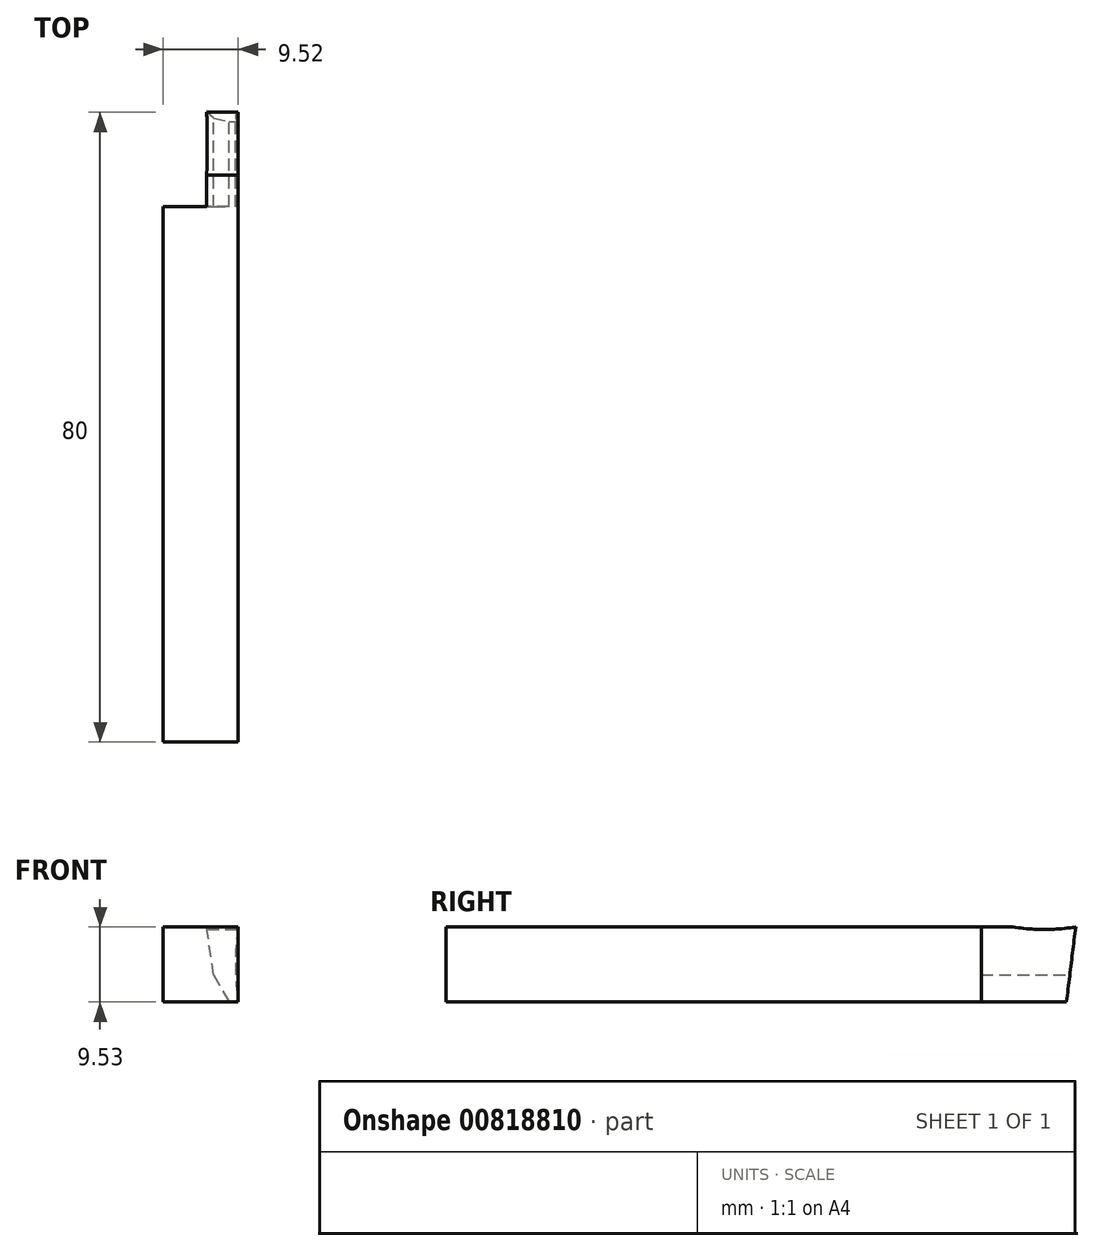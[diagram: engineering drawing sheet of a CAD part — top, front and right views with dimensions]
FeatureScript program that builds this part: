
annotation { "Feature Type Name" : "Feature", "Feature Type Description" : "" }
export const myFeature = defineFeature(function(context is Context, id is Id, definition is map)
    precondition{}
    {
        {
            var Q0;
            Q0=qCreatedBy(makeId("Front.planeOp"),FACE);
            var sketch = newSketch(context, id + "F0", { "sketchPlane" : qUnion([Q0])});
            skCircle(sketch, "E0", {"center": v(0, 0) * mm, "radius": 51 * mm});
            skCircle(sketch, "E1", {"center": v(0, 0) * mm, "radius": 57.5 * mm});
            skLineSegment(sketch, "E2.bottom", {"start": v(-56.25, 0) * mm, "end": v(-52.25, 0) * mm});
            skLineSegment(sketch, "E2.top", {"start": v(-54.91, -9.53) * mm, "end": v(-52.25, -9.53) * mm});
            skLineSegment(sketch, "E3", {"start": v(-56.25, 0) * mm, "end": v(-54.91, -9.53) * mm});
            skCircle(sketch, "E4", {"center": v(0, 0) * mm, "radius": 56.25 * mm, "construction": true});
            skArc(sketch, "E5", {"start": v(-52.25, 0) * mm, "mid": v(-52.6, -4.76) * mm, "end": v(-52.25, -9.53) * mm});
            skLineSegment(sketch, "E6", {"start": v(-55.4, -6.1) * mm, "end": v(-53.41, -9.53) * mm});
            skCircle(sketch, "E7", {"center": v(0, 0) * mm, "radius": 52.25 * mm, "construction": true});
            skSolve(sketch);
        }
        {
            var Q0;
            Q0=makeQuery(id+"F0.imprint","IMPRINT",FACE,{"disambiguationData":[TD([[makeQuery(id+"F0.imprint","IMPRINT",EDGE,{"derivedFrom":sQuery(id+"F0.wireOp",EDGE,"E2.bottom")}),-1.0]])]});
            extrude(context, id + "F1", {"entities" : qUnion([Q0]), "depth" : 12 * mm, "offsetDistance" : 25 * mm});
        }
        {
            var Q0;
            Q0=makeQuery(id+"F1.opExtrude","CAP_FACE",FACE,{"disambiguationData":[OSD([sQuery(id+"F0.wireOp",EDGE,"E2.bottom"),sQuery(id+"F0.wireOp",EDGE,"E2.top"),sQuery(id+"F0.wireOp",EDGE,"E3"),sQuery(id+"F0.wireOp",EDGE,"E5")])],"isStart":false});
            var sketch = newSketch(context, id + "F2", { "sketchPlane" : qUnion([Q0])});
            skLineSegment(sketch, "E8.bottom", {"start": v(-52.25, -9.53) * mm, "end": v(-61.77, -9.53) * mm});
            skLineSegment(sketch, "E8.top", {"start": v(-52.25, 0) * mm, "end": v(-61.77, 0) * mm});
            skLineSegment(sketch, "E8.left", {"start": v(-52.25, -9.53) * mm, "end": v(-52.25, 0) * mm});
            skLineSegment(sketch, "E8.right", {"start": v(-61.77, -9.53) * mm, "end": v(-61.77, 0) * mm});
            skSolve(sketch);
        }
        {
            var Q0;
            Q0=qSketchRegion(id+"F2",true);
            extrude(context, id + "F3", {"entities" : qUnion([Q0]), "operationType" : NewBodyOperationType.ADD, "depth" : 68 * mm, "offsetDistance" : 25 * mm});
        }
        {
            var Q0;
            Q0=qCreatedBy(makeId("Right.planeOp"),FACE);
            var sketch = newSketch(context, id + "F4", { "sketchPlane" : qUnion([Q0])});
            skLineSegment(sketch, "E9", {"start": v(0, 0) * mm, "end": v(-1.17, -9.53) * mm});
            skLineSegment(sketch, "E10", {"start": v(-1.17, -9.53) * mm, "end": v(0, -9.53) * mm});
            skLineSegment(sketch, "E11", {"start": v(0, -9.53) * mm, "end": v(0, 0) * mm});
            skSolve(sketch);
        }
        {
            var Q0;
            Q0=qSketchRegion(id+"F4",true);
            var Q1;
            Q1=makeQuery(id+"F1.opExtrude","SWEPT_FACE",FACE,{"disambiguationData":[OSD([sQuery(id+"F0.wireOp",EDGE,"E3")])]});
            extrude(context, id + "F5", {"entities" : qUnion([Q0]), "operationType" : NewBodyOperationType.REMOVE, "endBound" : BoundingType.UP_TO_SURFACE, "oppositeDirection" : true, "depth" : 25 * mm, "endBoundEntityFace" : qUnion([Q1]), "offsetDistance" : 25 * mm});
        }
        {
            var Q0;
            Q0=qCreatedBy(makeId("Right.planeOp"),FACE);
            var sketch = newSketch(context, id + "F6", { "sketchPlane" : qUnion([Q0])});
            skLineSegment(sketch, "E12", {"start": v(-8, 0) * mm, "end": v(0, 0) * mm});
            skArc(sketch, "E13.filletArc", {"start": v(-8, 0) * mm, "mid": v(-4, -0.3) * mm, "end": v(0, 0) * mm});
            skLineSegment(sketch, "E14", {"start": v(-4, 0) * mm, "end": v(-4, -0.3) * mm});
            skSolve(sketch);
        }
        {
            var Q0;
            Q0=qSketchRegion(id+"F6",true);
            var Q1;
            Q1=makeQuery(id+"F1.opExtrude","SWEPT_FACE",FACE,{"disambiguationData":[OSD([sQuery(id+"F0.wireOp",EDGE,"E3")])]});
            extrude(context, id + "F7", {"entities" : qUnion([Q0]), "operationType" : NewBodyOperationType.REMOVE, "endBound" : BoundingType.UP_TO_SURFACE, "oppositeDirection" : true, "depth" : 25 * mm, "endBoundEntityFace" : qUnion([Q1]), "offsetDistance" : 25 * mm});
        }
    });
